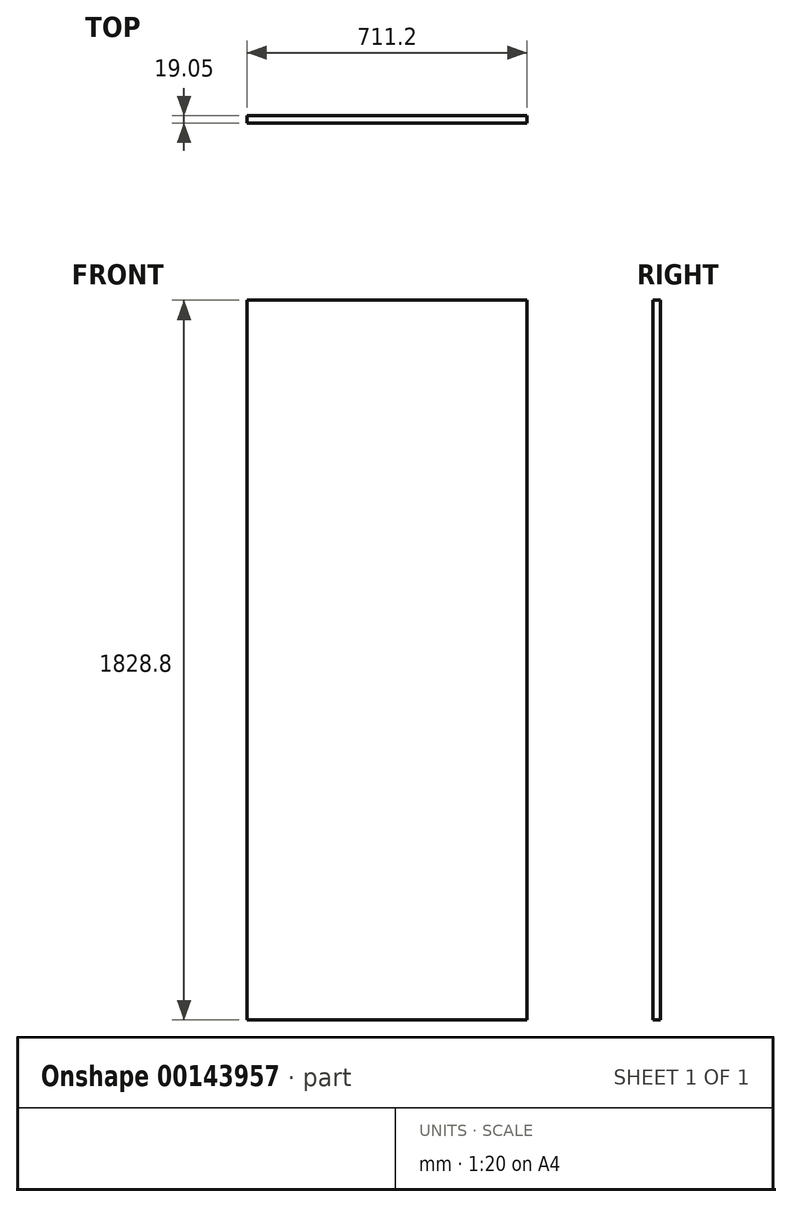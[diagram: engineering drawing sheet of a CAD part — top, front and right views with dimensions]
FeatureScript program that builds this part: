
annotation { "Feature Type Name" : "Feature", "Feature Type Description" : "" }
export const myFeature = defineFeature(function(context is Context, id is Id, definition is map)
    precondition{}
    {
        {
            var Q0;
            Q0=qCreatedBy(makeId("Front.planeOp"),FACE);
            var sketch = newSketch(context, id + "F0", { "sketchPlane" : qUnion([Q0])});
            skLineSegment(sketch, "E0.bottom", {"start": v(0, 0) * mm, "end": v(711.2, 0) * mm});
            skLineSegment(sketch, "E0.top", {"start": v(0, 1828.8) * mm, "end": v(711.2, 1828.8) * mm});
            skLineSegment(sketch, "E0.left", {"start": v(0, 0) * mm, "end": v(0, 1828.8) * mm});
            skLineSegment(sketch, "E0.right", {"start": v(711.2, 0) * mm, "end": v(711.2, 1828.8) * mm});
            skSolve(sketch);
        }
        {
            var Q0;
            Q0=makeQuery(id+"F0.imprint","IMPRINT",FACE,{"disambiguationData":[TD([[makeQuery(id+"F0.imprint","IMPRINT",EDGE,{"derivedFrom":sQuery(id+"F0.wireOp",EDGE,"E0.bottom")}),1.0]])]});
            extrude(context, id + "F1", {"entities" : qUnion([Q0]), "depth" : 19.05 * mm});
        }
    });
